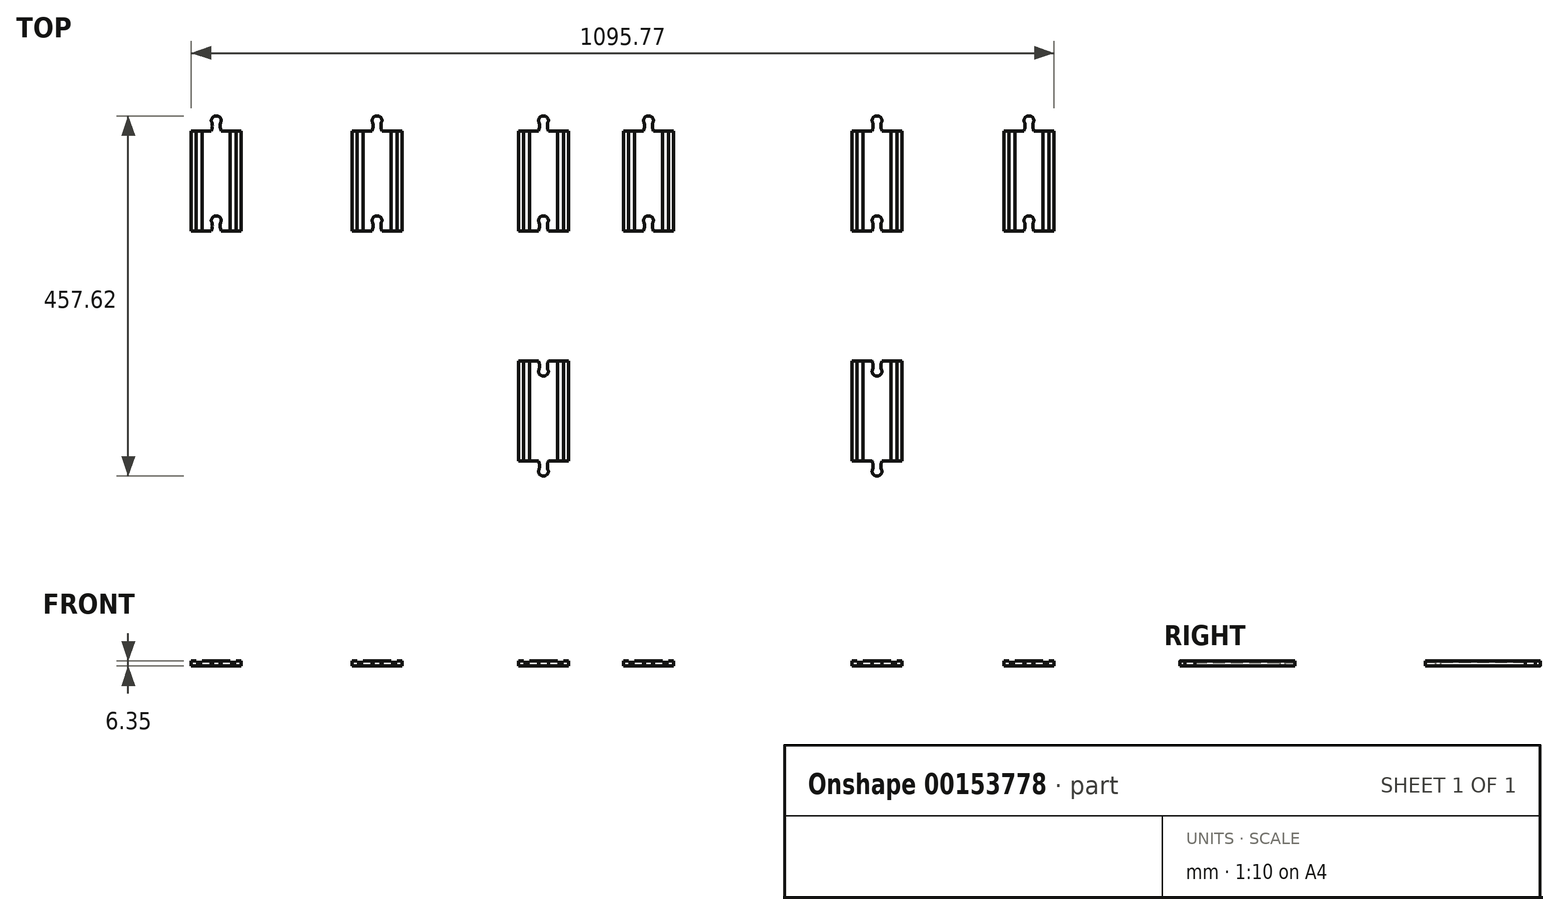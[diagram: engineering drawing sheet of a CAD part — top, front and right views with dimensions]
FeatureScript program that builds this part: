
annotation { "Feature Type Name" : "Feature", "Feature Type Description" : "" }
export const myFeature = defineFeature(function(context is Context, id is Id, definition is map)
    precondition{}
    {
        {
            var Q0;
            Q0=qCreatedBy(makeId("Top.planeOp"),FACE);
            var sketch = newSketch(context, id + "F0", { "sketchPlane" : qUnion([Q0])});
            skLineSegment(sketch, "E0", {"start": v(-44.88, 90.72) * mm, "end": v(-44.88, -36.28) * mm});
            skLineSegment(sketch, "E1", {"start": v(-44.88, -36.28) * mm, "end": v(-19.48, -36.28) * mm});
            skLineSegment(sketch, "E2", {"start": v(18.62, -36.28) * mm, "end": v(18.62, 90.72) * mm});
            skLineSegment(sketch, "E3", {"start": v(18.62, 90.72) * mm, "end": v(-6.78, 90.72) * mm});
            skArc(sketch, "E4", {"start": v(-6.78, 103.42) * mm, "mid": v(-13.13, 109.77) * mm, "end": v(-19.48, 103.42) * mm});
            skArc(sketch, "E5", {"start": v(-6.78, 103.42) * mm, "mid": v(-8.16, 97.07) * mm, "end": v(-6.78, 90.72) * mm});
            skArc(sketch, "E6.MirrorCS", {"start": v(-19.48, 103.42) * mm, "mid": v(-18.09, 97.07) * mm, "end": v(-19.48, 90.72) * mm});
            skArc(sketch, "E7", {"start": v(-6.78, -23.58) * mm, "mid": v(-13.13, -17.23) * mm, "end": v(-19.48, -23.58) * mm});
            skPoint(sketch, "E8.start.orphan", {"position": v(-13.13, -36.28) * mm});
            skArc(sketch, "E9", {"start": v(-6.78, -23.58) * mm, "mid": v(-8.16, -29.93) * mm, "end": v(-6.78, -36.28) * mm});
            skArc(sketch, "E10.MirrorCS", {"start": v(-19.48, -23.58) * mm, "mid": v(-18.09, -29.93) * mm, "end": v(-19.48, -36.28) * mm});
            skLineSegment(sketch, "E11.trimOffspring", {"start": v(-6.78, -36.28) * mm, "end": v(18.62, -36.28) * mm});
            skArc(sketch, "E12.MirrorCS", {"start": v(80.5, 103.42) * mm, "mid": v(81.9, 97.07) * mm, "end": v(80.5, 90.72) * mm});
            skLineSegment(sketch, "E13.MirrorCS", {"start": v(55.1, 90.72) * mm, "end": v(80.5, 90.72) * mm});
            skLineSegment(sketch, "E14.MirrorCS", {"start": v(118.6, 90.72) * mm, "end": v(118.6, -36.28) * mm});
            skLineSegment(sketch, "E15.MirrorCS", {"start": v(80.5, -36.28) * mm, "end": v(55.1, -36.28) * mm});
            skPoint(sketch, "E16.MirrorP", {"position": v(86.86, -36.28) * mm});
            skArc(sketch, "E17.MirrorCS", {"start": v(80.5, -23.58) * mm, "mid": v(81.9, -29.93) * mm, "end": v(80.5, -36.28) * mm});
            skArc(sketch, "E18.MirrorCS", {"start": v(80.5, 103.42) * mm, "mid": v(86.86, 109.77) * mm, "end": v(93.2, 103.42) * mm});
            skLineSegment(sketch, "E19.MirrorCS", {"start": v(55.1, -36.28) * mm, "end": v(55.1, 90.72) * mm});
            skArc(sketch, "E20.MirrorCS", {"start": v(93.2, -23.58) * mm, "mid": v(91.82, -29.93) * mm, "end": v(93.2, -36.28) * mm});
            skArc(sketch, "E21.MirrorCS", {"start": v(80.5, -23.58) * mm, "mid": v(86.86, -17.23) * mm, "end": v(93.2, -23.58) * mm});
            skLineSegment(sketch, "E22.MirrorCS", {"start": v(118.6, -36.28) * mm, "end": v(93.2, -36.28) * mm});
            skArc(sketch, "E23.MirrorCS", {"start": v(93.2, 103.42) * mm, "mid": v(91.82, 97.07) * mm, "end": v(93.2, 90.72) * mm});
            skArc(sketch, "E24.MirrorCS", {"start": v(197.37, -23.58) * mm, "mid": v(195.98, -29.93) * mm, "end": v(197.37, -36.28) * mm});
            skArc(sketch, "E25.MirrorCS", {"start": v(184.67, -23.58) * mm, "mid": v(186.06, -29.93) * mm, "end": v(184.67, -36.28) * mm});
            skArc(sketch, "E26.MirrorCS", {"start": v(184.67, 103.42) * mm, "mid": v(186.06, 97.07) * mm, "end": v(184.67, 90.72) * mm});
            skArc(sketch, "E27.MirrorCS", {"start": v(197.37, -23.58) * mm, "mid": v(191.02, -17.23) * mm, "end": v(184.67, -23.58) * mm});
            skArc(sketch, "E28.MirrorCS", {"start": v(197.37, 103.42) * mm, "mid": v(195.98, 97.07) * mm, "end": v(197.37, 90.72) * mm});
            skLineSegment(sketch, "E29.MirrorCS", {"start": v(197.37, -36.28) * mm, "end": v(222.77, -36.28) * mm});
            skArc(sketch, "E30.MirrorCS", {"start": v(197.37, 103.42) * mm, "mid": v(191.02, 109.77) * mm, "end": v(184.67, 103.42) * mm});
            skLineSegment(sketch, "E31.MirrorCS", {"start": v(159.27, -36.28) * mm, "end": v(184.67, -36.28) * mm});
            skLineSegment(sketch, "E32.MirrorCS", {"start": v(222.77, 90.72) * mm, "end": v(197.37, 90.72) * mm});
            skLineSegment(sketch, "E33.MirrorCS", {"start": v(222.77, -36.28) * mm, "end": v(222.77, 90.72) * mm});
            skPoint(sketch, "E34.MirrorP", {"position": v(191.02, -36.28) * mm});
            skLineSegment(sketch, "E35.MirrorCS", {"start": v(159.27, 90.72) * mm, "end": v(159.27, -36.28) * mm});
            skArc(sketch, "E36.MirrorCS", {"start": v(408.77, -23.58) * mm, "mid": v(407.39, -29.93) * mm, "end": v(408.77, -36.28) * mm});
            skArc(sketch, "E37.MirrorCS", {"start": v(396.07, -23.58) * mm, "mid": v(397.46, -29.93) * mm, "end": v(396.07, -36.28) * mm});
            skArc(sketch, "E38.MirrorCS", {"start": v(396.07, 103.42) * mm, "mid": v(402.42, 109.77) * mm, "end": v(408.77, 103.42) * mm});
            skLineSegment(sketch, "E39.MirrorCS", {"start": v(396.07, -36.28) * mm, "end": v(370.67, -36.28) * mm});
            skLineSegment(sketch, "E40.MirrorCS", {"start": v(434.17, -36.28) * mm, "end": v(408.77, -36.28) * mm});
            skArc(sketch, "E41.MirrorCS", {"start": v(396.07, -23.58) * mm, "mid": v(402.42, -17.23) * mm, "end": v(408.77, -23.58) * mm});
            skArc(sketch, "E42.MirrorCS", {"start": v(408.77, 103.42) * mm, "mid": v(407.39, 97.07) * mm, "end": v(408.77, 90.72) * mm});
            skArc(sketch, "E43.MirrorCS", {"start": v(396.07, 103.42) * mm, "mid": v(397.46, 97.07) * mm, "end": v(396.07, 90.72) * mm});
            skLineSegment(sketch, "E44.MirrorCS", {"start": v(370.67, 90.72) * mm, "end": v(396.07, 90.72) * mm});
            skLineSegment(sketch, "E45.MirrorCS", {"start": v(370.67, -36.28) * mm, "end": v(370.67, 90.72) * mm});
            skPoint(sketch, "E46.MirrorP", {"position": v(402.42, -36.28) * mm});
            skLineSegment(sketch, "E47.MirrorCS", {"start": v(434.17, 90.72) * mm, "end": v(434.17, -36.28) * mm});
            skArc(sketch, "E48.MirrorCS", {"start": v(542.2, 103.42) * mm, "mid": v(540.8, 97.07) * mm, "end": v(542.2, 90.72) * mm});
            skArc(sketch, "E49.MirrorCS", {"start": v(542.2, -23.58) * mm, "mid": v(540.8, -29.93) * mm, "end": v(542.2, -36.28) * mm});
            skArc(sketch, "E50.MirrorCS", {"start": v(542.2, 103.42) * mm, "mid": v(535.84, 109.77) * mm, "end": v(529.5, 103.42) * mm});
            skArc(sketch, "E51.MirrorCS", {"start": v(529.5, 103.42) * mm, "mid": v(530.88, 97.07) * mm, "end": v(529.5, 90.72) * mm});
            skArc(sketch, "E52.MirrorCS", {"start": v(529.5, -23.58) * mm, "mid": v(530.88, -29.93) * mm, "end": v(529.5, -36.28) * mm});
            skLineSegment(sketch, "E53.MirrorCS", {"start": v(567.6, 90.72) * mm, "end": v(542.2, 90.72) * mm});
            skArc(sketch, "E54.MirrorCS", {"start": v(542.2, -23.58) * mm, "mid": v(535.84, -17.23) * mm, "end": v(529.5, -23.58) * mm});
            skLineSegment(sketch, "E55.MirrorCS", {"start": v(504.1, -36.28) * mm, "end": v(529.5, -36.28) * mm});
            skLineSegment(sketch, "E56.MirrorCS", {"start": v(542.2, -36.28) * mm, "end": v(567.6, -36.28) * mm});
            skLineSegment(sketch, "E57.MirrorCS", {"start": v(504.1, 90.72) * mm, "end": v(504.1, -36.28) * mm});
            skLineSegment(sketch, "E58.MirrorCS", {"start": v(567.6, -36.28) * mm, "end": v(567.6, 90.72) * mm});
            skPoint(sketch, "E59.MirrorP", {"position": v(535.84, -36.28) * mm});
            skArc(sketch, "E60.MirrorCS", {"start": v(832.53, -23.58) * mm, "mid": v(831.14, -29.93) * mm, "end": v(832.53, -36.28) * mm});
            skArc(sketch, "E61.MirrorCS", {"start": v(819.83, -23.58) * mm, "mid": v(821.22, -29.93) * mm, "end": v(819.83, -36.28) * mm});
            skArc(sketch, "E62.MirrorCS", {"start": v(819.83, -23.58) * mm, "mid": v(826.18, -17.23) * mm, "end": v(832.53, -23.58) * mm});
            skLineSegment(sketch, "E63.MirrorCS", {"start": v(857.93, -36.28) * mm, "end": v(832.53, -36.28) * mm});
            skArc(sketch, "E64.MirrorCS", {"start": v(819.83, 103.42) * mm, "mid": v(821.22, 97.07) * mm, "end": v(819.83, 90.72) * mm});
            skArc(sketch, "E65.MirrorCS", {"start": v(832.53, 103.42) * mm, "mid": v(831.14, 97.07) * mm, "end": v(832.53, 90.72) * mm});
            skArc(sketch, "E66.MirrorCS", {"start": v(819.83, 103.42) * mm, "mid": v(826.18, 109.77) * mm, "end": v(832.53, 103.42) * mm});
            skLineSegment(sketch, "E67.MirrorCS", {"start": v(819.83, -36.28) * mm, "end": v(794.43, -36.28) * mm});
            skLineSegment(sketch, "E68.MirrorCS", {"start": v(794.43, 90.72) * mm, "end": v(819.83, 90.72) * mm});
            skPoint(sketch, "E69.MirrorP", {"position": v(826.18, -36.28) * mm});
            skLineSegment(sketch, "E70.MirrorCS", {"start": v(857.93, 90.72) * mm, "end": v(857.93, -36.28) * mm});
            skLineSegment(sketch, "E71.MirrorCS", {"start": v(794.43, -36.28) * mm, "end": v(794.43, 90.72) * mm});
            skArc(sketch, "E72.MirrorCS", {"start": v(819.83, -341.5) * mm, "mid": v(821.22, -335.15) * mm, "end": v(819.83, -328.8) * mm});
            skArc(sketch, "E73.MirrorCS", {"start": v(396.07, -214.5) * mm, "mid": v(397.46, -208.15) * mm, "end": v(396.07, -201.8) * mm});
            skArc(sketch, "E74.MirrorCS", {"start": v(93.2, -214.5) * mm, "mid": v(91.82, -208.15) * mm, "end": v(93.2, -201.8) * mm});
            skArc(sketch, "E75.MirrorCS", {"start": v(832.53, -341.5) * mm, "mid": v(831.14, -335.15) * mm, "end": v(832.53, -328.8) * mm});
            skArc(sketch, "E76.MirrorCS", {"start": v(408.77, -214.5) * mm, "mid": v(407.39, -208.15) * mm, "end": v(408.77, -201.8) * mm});
            skArc(sketch, "E77.MirrorCS", {"start": v(197.37, -214.5) * mm, "mid": v(191.02, -220.85) * mm, "end": v(184.67, -214.5) * mm});
            skArc(sketch, "E78.MirrorCS", {"start": v(80.5, -214.5) * mm, "mid": v(86.86, -220.85) * mm, "end": v(93.2, -214.5) * mm});
            skArc(sketch, "E79.MirrorCS", {"start": v(819.83, -341.5) * mm, "mid": v(826.18, -347.85) * mm, "end": v(832.53, -341.5) * mm});
            skArc(sketch, "E80.MirrorCS", {"start": v(819.83, -214.5) * mm, "mid": v(821.22, -208.15) * mm, "end": v(819.83, -201.8) * mm});
            skArc(sketch, "E81.MirrorCS", {"start": v(542.2, -214.5) * mm, "mid": v(540.8, -208.15) * mm, "end": v(542.2, -201.8) * mm});
            skArc(sketch, "E82.MirrorCS", {"start": v(197.37, -214.5) * mm, "mid": v(195.98, -208.15) * mm, "end": v(197.37, -201.8) * mm});
            skArc(sketch, "E83.MirrorCS", {"start": v(80.5, -214.5) * mm, "mid": v(81.9, -208.15) * mm, "end": v(80.5, -201.8) * mm});
            skArc(sketch, "E84.MirrorCS", {"start": v(832.53, -214.5) * mm, "mid": v(831.14, -208.15) * mm, "end": v(832.53, -201.8) * mm});
            skArc(sketch, "E85.MirrorCS", {"start": v(184.67, -214.5) * mm, "mid": v(186.06, -208.15) * mm, "end": v(184.67, -201.8) * mm});
            skArc(sketch, "E86.MirrorCS", {"start": v(529.5, -214.5) * mm, "mid": v(530.88, -208.15) * mm, "end": v(529.5, -201.8) * mm});
            skLineSegment(sketch, "E87.MirrorCS", {"start": v(197.37, -201.8) * mm, "end": v(222.77, -201.8) * mm});
            skArc(sketch, "E88.MirrorCS", {"start": v(542.2, -214.5) * mm, "mid": v(535.84, -220.85) * mm, "end": v(529.5, -214.5) * mm});
            skArc(sketch, "E89.MirrorCS", {"start": v(197.37, -341.5) * mm, "mid": v(195.98, -335.15) * mm, "end": v(197.37, -328.8) * mm});
            skLineSegment(sketch, "E90.MirrorCS", {"start": v(857.93, -201.8) * mm, "end": v(832.53, -201.8) * mm});
            skArc(sketch, "E91.MirrorCS", {"start": v(80.5, -341.5) * mm, "mid": v(86.86, -347.85) * mm, "end": v(93.2, -341.5) * mm});
            skLineSegment(sketch, "E92.MirrorCS", {"start": v(504.1, -201.8) * mm, "end": v(529.5, -201.8) * mm});
            skArc(sketch, "E93.MirrorCS", {"start": v(396.07, -341.5) * mm, "mid": v(402.42, -347.85) * mm, "end": v(408.77, -341.5) * mm});
            skArc(sketch, "E94.MirrorCS", {"start": v(542.2, -341.5) * mm, "mid": v(540.8, -335.15) * mm, "end": v(542.2, -328.8) * mm});
            skArc(sketch, "E95.MirrorCS", {"start": v(197.37, -341.5) * mm, "mid": v(191.02, -347.85) * mm, "end": v(184.67, -341.5) * mm});
            skLineSegment(sketch, "E96.MirrorCS", {"start": v(567.6, -328.8) * mm, "end": v(542.2, -328.8) * mm});
            skLineSegment(sketch, "E97.MirrorCS", {"start": v(370.67, -328.8) * mm, "end": v(396.07, -328.8) * mm});
            skArc(sketch, "E98.MirrorCS", {"start": v(819.83, -214.5) * mm, "mid": v(826.18, -220.85) * mm, "end": v(832.53, -214.5) * mm});
            skLineSegment(sketch, "E99.MirrorCS", {"start": v(396.07, -201.8) * mm, "end": v(370.67, -201.8) * mm});
            skLineSegment(sketch, "E100.MirrorCS", {"start": v(542.2, -201.8) * mm, "end": v(567.6, -201.8) * mm});
            skArc(sketch, "E101.MirrorCS", {"start": v(93.2, -341.5) * mm, "mid": v(91.82, -335.15) * mm, "end": v(93.2, -328.8) * mm});
            skArc(sketch, "E102.MirrorCS", {"start": v(396.07, -341.5) * mm, "mid": v(397.46, -335.15) * mm, "end": v(396.07, -328.8) * mm});
            skLineSegment(sketch, "E103.MirrorCS", {"start": v(794.43, -328.8) * mm, "end": v(819.83, -328.8) * mm});
            skArc(sketch, "E104.MirrorCS", {"start": v(529.5, -341.5) * mm, "mid": v(530.88, -335.15) * mm, "end": v(529.5, -328.8) * mm});
            skArc(sketch, "E105.MirrorCS", {"start": v(184.67, -341.5) * mm, "mid": v(186.06, -335.15) * mm, "end": v(184.67, -328.8) * mm});
            skArc(sketch, "E106.MirrorCS", {"start": v(396.07, -214.5) * mm, "mid": v(402.42, -220.85) * mm, "end": v(408.77, -214.5) * mm});
            skLineSegment(sketch, "E107.MirrorCS", {"start": v(55.1, -328.8) * mm, "end": v(80.5, -328.8) * mm});
            skLineSegment(sketch, "E108.MirrorCS", {"start": v(159.27, -201.8) * mm, "end": v(184.67, -201.8) * mm});
            skLineSegment(sketch, "E109.MirrorCS", {"start": v(80.5, -201.8) * mm, "end": v(55.1, -201.8) * mm});
            skLineSegment(sketch, "E110.MirrorCS", {"start": v(434.17, -201.8) * mm, "end": v(408.77, -201.8) * mm});
            skLineSegment(sketch, "E111.MirrorCS", {"start": v(819.83, -201.8) * mm, "end": v(794.43, -201.8) * mm});
            skArc(sketch, "E112.MirrorCS", {"start": v(408.77, -341.5) * mm, "mid": v(407.39, -335.15) * mm, "end": v(408.77, -328.8) * mm});
            skLineSegment(sketch, "E113.MirrorCS", {"start": v(222.77, -328.8) * mm, "end": v(197.37, -328.8) * mm});
            skArc(sketch, "E114.MirrorCS", {"start": v(80.5, -341.5) * mm, "mid": v(81.9, -335.15) * mm, "end": v(80.5, -328.8) * mm});
            skLineSegment(sketch, "E115.MirrorCS", {"start": v(118.6, -201.8) * mm, "end": v(93.2, -201.8) * mm});
            skArc(sketch, "E116.MirrorCS", {"start": v(542.2, -341.5) * mm, "mid": v(535.84, -347.85) * mm, "end": v(529.5, -341.5) * mm});
            skLineSegment(sketch, "E117.MirrorCS", {"start": v(434.17, -328.8) * mm, "end": v(434.17, -201.8) * mm});
            skLineSegment(sketch, "E118.MirrorCS", {"start": v(55.1, -201.8) * mm, "end": v(55.1, -328.8) * mm});
            skLineSegment(sketch, "E119.MirrorCS", {"start": v(370.67, -201.8) * mm, "end": v(370.67, -328.8) * mm});
            skPoint(sketch, "E120.MirrorP", {"position": v(86.86, -201.8) * mm});
            skLineSegment(sketch, "E121.MirrorCS", {"start": v(794.43, -201.8) * mm, "end": v(794.43, -328.8) * mm});
            skPoint(sketch, "E122.MirrorP", {"position": v(191.02, -201.8) * mm});
            skPoint(sketch, "E123.MirrorP", {"position": v(535.84, -201.8) * mm});
            skPoint(sketch, "E124.MirrorP", {"position": v(402.42, -201.8) * mm});
            skLineSegment(sketch, "E125.MirrorCS", {"start": v(567.6, -201.8) * mm, "end": v(567.6, -328.8) * mm});
            skLineSegment(sketch, "E126.MirrorCS", {"start": v(222.77, -201.8) * mm, "end": v(222.77, -328.8) * mm});
            skLineSegment(sketch, "E127.MirrorCS", {"start": v(118.6, -328.8) * mm, "end": v(118.6, -201.8) * mm});
            skPoint(sketch, "E128.MirrorP", {"position": v(826.18, -201.8) * mm});
            skLineSegment(sketch, "E129.MirrorCS", {"start": v(504.1, -328.8) * mm, "end": v(504.1, -201.8) * mm});
            skLineSegment(sketch, "E130.MirrorCS", {"start": v(159.27, -328.8) * mm, "end": v(159.27, -201.8) * mm});
            skLineSegment(sketch, "E131.MirrorCS", {"start": v(857.93, -328.8) * mm, "end": v(857.93, -201.8) * mm});
            skArc(sketch, "E132.MirrorCS", {"start": v(-6.78, -341.5) * mm, "mid": v(-13.13, -347.85) * mm, "end": v(-19.48, -341.5) * mm});
            skArc(sketch, "E133.MirrorCS", {"start": v(-19.48, -214.5) * mm, "mid": v(-18.09, -208.15) * mm, "end": v(-19.48, -201.8) * mm});
            skArc(sketch, "E134.MirrorCS", {"start": v(-6.78, -214.5) * mm, "mid": v(-13.13, -220.85) * mm, "end": v(-19.48, -214.5) * mm});
            skLineSegment(sketch, "E135.MirrorCS", {"start": v(-6.78, -201.8) * mm, "end": v(18.62, -201.8) * mm});
            skArc(sketch, "E136.MirrorCS", {"start": v(-6.78, -214.5) * mm, "mid": v(-8.16, -208.15) * mm, "end": v(-6.78, -201.8) * mm});
            skArc(sketch, "E137.MirrorCS", {"start": v(-19.48, -341.5) * mm, "mid": v(-18.09, -335.15) * mm, "end": v(-19.48, -328.8) * mm});
            skArc(sketch, "E138.MirrorCS", {"start": v(-6.78, -341.5) * mm, "mid": v(-8.16, -335.15) * mm, "end": v(-6.78, -328.8) * mm});
            skLineSegment(sketch, "E139.MirrorCS", {"start": v(18.62, -328.8) * mm, "end": v(-6.78, -328.8) * mm});
            skLineSegment(sketch, "E140.MirrorCS", {"start": v(-44.88, -201.8) * mm, "end": v(-19.48, -201.8) * mm});
            skLineSegment(sketch, "E141.MirrorCS", {"start": v(18.62, -201.8) * mm, "end": v(18.62, -328.8) * mm});
            skLineSegment(sketch, "E142.MirrorCS", {"start": v(-44.88, -328.8) * mm, "end": v(-44.88, -201.8) * mm});
            skPoint(sketch, "E143.MirrorP", {"position": v(-13.13, -201.8) * mm});
            skLineSegment(sketch, "E144.trimOffspring", {"start": v(-19.48, 90.72) * mm, "end": v(-44.88, 90.72) * mm});
            skLineSegment(sketch, "E145.trimOffspring", {"start": v(93.2, 90.72) * mm, "end": v(118.6, 90.72) * mm});
            skLineSegment(sketch, "E146.trimOffspring", {"start": v(184.67, 90.72) * mm, "end": v(159.27, 90.72) * mm});
            skLineSegment(sketch, "E147.trimOffspring", {"start": v(408.77, 90.72) * mm, "end": v(434.17, 90.72) * mm});
            skLineSegment(sketch, "E148.trimOffspring", {"start": v(529.5, 90.72) * mm, "end": v(504.1, 90.72) * mm});
            skLineSegment(sketch, "E149.trimOffspring", {"start": v(832.53, 90.72) * mm, "end": v(857.93, 90.72) * mm});
            skLineSegment(sketch, "E150.trimOffspring", {"start": v(832.53, -328.8) * mm, "end": v(857.93, -328.8) * mm});
            skLineSegment(sketch, "E151.trimOffspring", {"start": v(529.5, -328.8) * mm, "end": v(504.1, -328.8) * mm});
            skLineSegment(sketch, "E152.trimOffspring", {"start": v(408.77, -328.8) * mm, "end": v(434.17, -328.8) * mm});
            skLineSegment(sketch, "E153.trimOffspring", {"start": v(184.67, -328.8) * mm, "end": v(159.27, -328.8) * mm});
            skLineSegment(sketch, "E154.trimOffspring", {"start": v(93.2, -328.8) * mm, "end": v(118.6, -328.8) * mm});
            skLineSegment(sketch, "E155.trimOffspring", {"start": v(-19.48, -328.8) * mm, "end": v(-44.88, -328.8) * mm});
            skLineSegment(sketch, "E156", {"start": v(922.66, 120.17) * mm, "end": v(922.66, -61.86) * mm});
            skArc(sketch, "E157.MirrorCS", {"start": v(1025.49, -23.58) * mm, "mid": v(1024.1, -29.93) * mm, "end": v(1025.49, -36.28) * mm});
            skArc(sketch, "E158.MirrorCS", {"start": v(1012.79, -23.58) * mm, "mid": v(1014.17, -29.93) * mm, "end": v(1012.79, -36.28) * mm});
            skArc(sketch, "E159.MirrorCS", {"start": v(1025.49, 103.42) * mm, "mid": v(1024.1, 97.07) * mm, "end": v(1025.49, 90.72) * mm});
            skArc(sketch, "E160.MirrorCS", {"start": v(1012.79, 103.42) * mm, "mid": v(1014.17, 97.07) * mm, "end": v(1012.79, 90.72) * mm});
            skLineSegment(sketch, "E161.MirrorCS", {"start": v(1025.49, -36.28) * mm, "end": v(1050.89, -36.28) * mm});
            skLineSegment(sketch, "E162.MirrorCS", {"start": v(1050.89, 90.72) * mm, "end": v(1025.49, 90.72) * mm});
            skArc(sketch, "E163.MirrorCS", {"start": v(1025.49, -23.58) * mm, "mid": v(1019.14, -17.23) * mm, "end": v(1012.79, -23.58) * mm});
            skArc(sketch, "E164.MirrorCS", {"start": v(1025.49, 103.42) * mm, "mid": v(1019.14, 109.77) * mm, "end": v(1012.79, 103.42) * mm});
            skLineSegment(sketch, "E165.MirrorCS", {"start": v(1012.79, 90.72) * mm, "end": v(987.39, 90.72) * mm});
            skLineSegment(sketch, "E166.MirrorCS", {"start": v(987.39, -36.28) * mm, "end": v(1012.79, -36.28) * mm});
            skPoint(sketch, "E167.MirrorP", {"position": v(1019.14, -36.28) * mm});
            skLineSegment(sketch, "E168.MirrorCS", {"start": v(987.39, 90.72) * mm, "end": v(987.39, -36.28) * mm});
            skLineSegment(sketch, "E169.MirrorCS", {"start": v(1050.89, -36.28) * mm, "end": v(1050.89, 90.72) * mm});
            skSolve(sketch);
        }
        {
            var Q0;
            Q0=makeQuery(id+"F0.imprint","IMPRINT",FACE,{"disambiguationData":[TD([[makeQuery(id+"F0.imprint","IMPRINT",EDGE,{"derivedFrom":sQuery(id+"F0.wireOp",EDGE,"E0")}),1.0]])]});
            var Q1;
            Q1=makeQuery(id+"F0.imprint","IMPRINT",FACE,{"disambiguationData":[TD([[makeQuery(id+"F0.imprint","IMPRINT",EDGE,{"derivedFrom":sQuery(id+"F0.wireOp",EDGE,"E12.MirrorCS")}),1.0]])]});
            var Q2;
            Q2=makeQuery(id+"F0.imprint","IMPRINT",FACE,{"disambiguationData":[TD([[makeQuery(id+"F0.imprint","IMPRINT",EDGE,{"derivedFrom":sQuery(id+"F0.wireOp",EDGE,"E24.MirrorCS")}),1.0]])]});
            var Q3;
            Q3=makeQuery(id+"F0.imprint","IMPRINT",FACE,{"disambiguationData":[TD([[makeQuery(id+"F0.imprint","IMPRINT",EDGE,{"derivedFrom":sQuery(id+"F0.wireOp",EDGE,"E36.MirrorCS")}),1.0]])]});
            var Q4;
            Q4=makeQuery(id+"F0.imprint","IMPRINT",FACE,{"disambiguationData":[TD([[makeQuery(id+"F0.imprint","IMPRINT",EDGE,{"derivedFrom":sQuery(id+"F0.wireOp",EDGE,"E48.MirrorCS")}),-1.0]])]});
            var Q5;
            Q5=makeQuery(id+"F0.imprint","IMPRINT",FACE,{"disambiguationData":[TD([[makeQuery(id+"F0.imprint","IMPRINT",EDGE,{"derivedFrom":sQuery(id+"F0.wireOp",EDGE,"E132.MirrorCS")}),-1.0]])]});
            var Q6;
            Q6=makeQuery(id+"F0.imprint","IMPRINT",FACE,{"disambiguationData":[TD([[makeQuery(id+"F0.imprint","IMPRINT",EDGE,{"derivedFrom":sQuery(id+"F0.wireOp",EDGE,"E74.MirrorCS")}),-1.0]])]});
            var Q7;
            Q7=makeQuery(id+"F0.imprint","IMPRINT",FACE,{"disambiguationData":[TD([[makeQuery(id+"F0.imprint","IMPRINT",EDGE,{"derivedFrom":sQuery(id+"F0.wireOp",EDGE,"E77.MirrorCS")}),1.0]])]});
            var Q8;
            Q8=makeQuery(id+"F0.imprint","IMPRINT",FACE,{"disambiguationData":[TD([[makeQuery(id+"F0.imprint","IMPRINT",EDGE,{"derivedFrom":sQuery(id+"F0.wireOp",EDGE,"E73.MirrorCS")}),1.0]])]});
            var Q9;
            Q9=makeQuery(id+"F0.imprint","IMPRINT",FACE,{"disambiguationData":[TD([[makeQuery(id+"F0.imprint","IMPRINT",EDGE,{"derivedFrom":sQuery(id+"F0.wireOp",EDGE,"E81.MirrorCS")}),-1.0]])]});
            var Q10;
            Q10=makeQuery(id+"F0.imprint","IMPRINT",FACE,{"disambiguationData":[TD([[makeQuery(id+"F0.imprint","IMPRINT",EDGE,{"derivedFrom":sQuery(id+"F0.wireOp",EDGE,"E60.MirrorCS")}),1.0]])]});
            var Q11;
            Q11=makeQuery(id+"F0.imprint","IMPRINT",FACE,{"disambiguationData":[TD([[makeQuery(id+"F0.imprint","IMPRINT",EDGE,{"derivedFrom":sQuery(id+"F0.wireOp",EDGE,"E72.MirrorCS")}),-1.0]])]});
            var Q12;
            Q12=makeQuery(id+"F0.imprint","IMPRINT",FACE,{"disambiguationData":[TD([[makeQuery(id+"F0.imprint","IMPRINT",EDGE,{"derivedFrom":sQuery(id+"F0.wireOp",EDGE,"E157.MirrorCS")}),1.0]])]});
            extrude(context, id + "F1", {"entities" : qUnion([Q0, Q1, Q2, Q3, Q4, Q5, Q6, Q7, Q8, Q9, Q10, Q11, Q12]), "depth" : 6.35 * mm});
        }
        {
            var Q0;
            Q0=makeQuery(id+"F1.opExtrude","CAP_FACE",FACE,{"disambiguationData":[OSD([sQuery(id+"F0.wireOp",EDGE,"E0"),sQuery(id+"F0.wireOp",EDGE,"E1"),sQuery(id+"F0.wireOp",EDGE,"E2"),sQuery(id+"F0.wireOp",EDGE,"E3"),sQuery(id+"F0.wireOp",EDGE,"E4"),sQuery(id+"F0.wireOp",EDGE,"E5"),sQuery(id+"F0.wireOp",EDGE,"E6.MirrorCS"),sQuery(id+"F0.wireOp",EDGE,"E7"),sQuery(id+"F0.wireOp",EDGE,"E9"),sQuery(id+"F0.wireOp",EDGE,"E10.MirrorCS"),sQuery(id+"F0.wireOp",EDGE,"E11.trimOffspring"),sQuery(id+"F0.wireOp",EDGE,"E144.trimOffspring")])],"isStart":false});
            var sketch = newSketch(context, id + "F2", { "sketchPlane" : qUnion([Q0])});
            skLineSegment(sketch, "E170.12", {"start": v(857.93, -328.8) * mm, "end": v(857.93, -201.8) * mm});
            skLineSegment(sketch, "E170.13", {"start": v(794.43, -201.8) * mm, "end": v(794.43, -328.8) * mm});
            skLineSegment(sketch, "E171.0", {"start": v(-38.53, 90.72) * mm, "end": v(-38.53, -36.28) * mm});
            skLineSegment(sketch, "E172.0", {"start": v(-30.9, 90.72) * mm, "end": v(-30.9, -36.28) * mm});
            skLineSegment(sketch, "E173", {"start": v(4.65, 90.72) * mm, "end": v(4.65, -36.28) * mm});
            skLineSegment(sketch, "E174", {"start": v(12.27, 90.72) * mm, "end": v(12.27, -36.28) * mm});
            skLineSegment(sketch, "E175", {"start": v(-38.53, -36.28) * mm, "end": v(-30.9, -36.28) * mm});
            skLineSegment(sketch, "E176", {"start": v(-30.9, 90.72) * mm, "end": v(-38.53, 90.72) * mm});
            skLineSegment(sketch, "E177", {"start": v(4.65, 90.72) * mm, "end": v(12.27, 90.72) * mm});
            skLineSegment(sketch, "E178", {"start": v(12.27, -36.28) * mm, "end": v(4.65, -36.28) * mm});
            skLineSegment(sketch, "E179.MirrorCS", {"start": v(61.46, 90.72) * mm, "end": v(61.46, -36.28) * mm});
            skLineSegment(sketch, "E180.MirrorCS", {"start": v(69.08, 90.72) * mm, "end": v(69.08, -36.28) * mm});
            skLineSegment(sketch, "E181.MirrorCS", {"start": v(61.46, -36.28) * mm, "end": v(69.08, -36.28) * mm});
            skLineSegment(sketch, "E182.MirrorCS", {"start": v(69.08, 90.72) * mm, "end": v(61.46, 90.72) * mm});
            skLineSegment(sketch, "E183.MirrorCS", {"start": v(112.26, -36.28) * mm, "end": v(104.64, -36.28) * mm});
            skLineSegment(sketch, "E184.MirrorCS", {"start": v(104.64, 90.72) * mm, "end": v(104.64, -36.28) * mm});
            skLineSegment(sketch, "E185.MirrorCS", {"start": v(112.26, 90.72) * mm, "end": v(112.26, -36.28) * mm});
            skLineSegment(sketch, "E186.MirrorCS", {"start": v(104.64, 90.72) * mm, "end": v(112.26, 90.72) * mm});
            skLineSegment(sketch, "E187.MirrorCS", {"start": v(165.62, 90.72) * mm, "end": v(165.62, -36.28) * mm});
            skLineSegment(sketch, "E188.MirrorCS", {"start": v(173.24, 90.72) * mm, "end": v(173.24, -36.28) * mm});
            skLineSegment(sketch, "E189.MirrorCS", {"start": v(208.8, 90.72) * mm, "end": v(208.8, -36.28) * mm});
            skLineSegment(sketch, "E190.MirrorCS", {"start": v(216.42, 90.72) * mm, "end": v(216.42, -36.28) * mm});
            skLineSegment(sketch, "E191.MirrorCS", {"start": v(173.24, 90.72) * mm, "end": v(165.62, 90.72) * mm});
            skLineSegment(sketch, "E192.MirrorCS", {"start": v(165.62, -36.28) * mm, "end": v(173.24, -36.28) * mm});
            skLineSegment(sketch, "E193.MirrorCS", {"start": v(216.42, -36.28) * mm, "end": v(208.8, -36.28) * mm});
            skLineSegment(sketch, "E194.MirrorCS", {"start": v(208.8, 90.72) * mm, "end": v(216.42, 90.72) * mm});
            skLineSegment(sketch, "E195.MirrorCS", {"start": v(377.02, 90.72) * mm, "end": v(377.02, -36.28) * mm});
            skLineSegment(sketch, "E196.MirrorCS", {"start": v(384.64, 90.72) * mm, "end": v(384.64, -36.28) * mm});
            skLineSegment(sketch, "E197.MirrorCS", {"start": v(420.2, 90.72) * mm, "end": v(420.2, -36.28) * mm});
            skLineSegment(sketch, "E198.MirrorCS", {"start": v(427.82, 90.72) * mm, "end": v(427.82, -36.28) * mm});
            skLineSegment(sketch, "E199.MirrorCS", {"start": v(420.2, 90.72) * mm, "end": v(427.82, 90.72) * mm});
            skLineSegment(sketch, "E200.MirrorCS", {"start": v(384.64, 90.72) * mm, "end": v(377.02, 90.72) * mm});
            skLineSegment(sketch, "E201.MirrorCS", {"start": v(377.02, -36.28) * mm, "end": v(384.64, -36.28) * mm});
            skLineSegment(sketch, "E202.MirrorCS", {"start": v(427.82, -36.28) * mm, "end": v(420.2, -36.28) * mm});
            skLineSegment(sketch, "E203.MirrorCS", {"start": v(510.44, 90.72) * mm, "end": v(510.44, -36.28) * mm});
            skLineSegment(sketch, "E204.MirrorCS", {"start": v(518.06, 90.72) * mm, "end": v(518.06, -36.28) * mm});
            skLineSegment(sketch, "E205.MirrorCS", {"start": v(518.06, 90.72) * mm, "end": v(510.44, 90.72) * mm});
            skLineSegment(sketch, "E206.MirrorCS", {"start": v(553.62, 90.72) * mm, "end": v(553.62, -36.28) * mm});
            skLineSegment(sketch, "E207.MirrorCS", {"start": v(561.24, 90.72) * mm, "end": v(561.24, -36.28) * mm});
            skLineSegment(sketch, "E208.MirrorCS", {"start": v(553.62, 90.72) * mm, "end": v(561.24, 90.72) * mm});
            skLineSegment(sketch, "E209.MirrorCS", {"start": v(800.78, 90.72) * mm, "end": v(800.78, -36.28) * mm});
            skLineSegment(sketch, "E210.MirrorCS", {"start": v(808.4, 90.72) * mm, "end": v(808.4, -36.28) * mm});
            skLineSegment(sketch, "E211.MirrorCS", {"start": v(808.4, 90.72) * mm, "end": v(800.78, 90.72) * mm});
            skLineSegment(sketch, "E212.MirrorCS", {"start": v(843.96, 90.72) * mm, "end": v(851.58, 90.72) * mm});
            skLineSegment(sketch, "E213.MirrorCS", {"start": v(843.96, 90.72) * mm, "end": v(843.96, -36.28) * mm});
            skLineSegment(sketch, "E214.MirrorCS", {"start": v(851.58, 90.72) * mm, "end": v(851.58, -36.28) * mm});
            skLineSegment(sketch, "E215", {"start": v(808.4, -36.28) * mm, "end": v(800.78, -36.28) * mm});
            skLineSegment(sketch, "E216", {"start": v(851.58, -36.28) * mm, "end": v(843.96, -36.28) * mm});
            skLineSegment(sketch, "E217", {"start": v(561.24, -36.28) * mm, "end": v(553.62, -36.28) * mm});
            skLineSegment(sketch, "E218", {"start": v(518.06, -36.28) * mm, "end": v(510.44, -36.28) * mm});
            skLineSegment(sketch, "E219.MirrorCS", {"start": v(427.82, -201.8) * mm, "end": v(420.2, -201.8) * mm});
            skLineSegment(sketch, "E220.MirrorCS", {"start": v(61.46, -201.8) * mm, "end": v(69.08, -201.8) * mm});
            skLineSegment(sketch, "E221.MirrorCS", {"start": v(-38.53, -201.8) * mm, "end": v(-30.9, -201.8) * mm});
            skLineSegment(sketch, "E222.MirrorCS", {"start": v(-30.9, -328.8) * mm, "end": v(-38.53, -328.8) * mm});
            skLineSegment(sketch, "E223.MirrorCS", {"start": v(165.62, -201.8) * mm, "end": v(173.24, -201.8) * mm});
            skLineSegment(sketch, "E224.MirrorCS", {"start": v(518.06, -201.8) * mm, "end": v(510.44, -201.8) * mm});
            skLineSegment(sketch, "E225.MirrorCS", {"start": v(518.06, -328.8) * mm, "end": v(510.44, -328.8) * mm});
            skLineSegment(sketch, "E226.MirrorCS", {"start": v(173.24, -328.8) * mm, "end": v(165.62, -328.8) * mm});
            skLineSegment(sketch, "E227.MirrorCS", {"start": v(851.58, -201.8) * mm, "end": v(843.96, -201.8) * mm});
            skLineSegment(sketch, "E228.MirrorCS", {"start": v(384.64, -328.8) * mm, "end": v(377.02, -328.8) * mm});
            skLineSegment(sketch, "E229.MirrorCS", {"start": v(420.2, -328.8) * mm, "end": v(427.82, -328.8) * mm});
            skLineSegment(sketch, "E230.MirrorCS", {"start": v(377.02, -201.8) * mm, "end": v(384.64, -201.8) * mm});
            skLineSegment(sketch, "E231.MirrorCS", {"start": v(208.8, -328.8) * mm, "end": v(216.42, -328.8) * mm});
            skLineSegment(sketch, "E232.MirrorCS", {"start": v(69.08, -328.8) * mm, "end": v(61.46, -328.8) * mm});
            skLineSegment(sketch, "E233.MirrorCS", {"start": v(808.4, -328.8) * mm, "end": v(800.78, -328.8) * mm});
            skLineSegment(sketch, "E234.MirrorCS", {"start": v(4.65, -328.8) * mm, "end": v(12.27, -328.8) * mm});
            skLineSegment(sketch, "E235.MirrorCS", {"start": v(112.26, -201.8) * mm, "end": v(104.64, -201.8) * mm});
            skLineSegment(sketch, "E236.MirrorCS", {"start": v(553.62, -328.8) * mm, "end": v(561.24, -328.8) * mm});
            skLineSegment(sketch, "E237.MirrorCS", {"start": v(104.64, -328.8) * mm, "end": v(112.26, -328.8) * mm});
            skLineSegment(sketch, "E238.MirrorCS", {"start": v(843.96, -328.8) * mm, "end": v(851.58, -328.8) * mm});
            skLineSegment(sketch, "E239.MirrorCS", {"start": v(216.42, -201.8) * mm, "end": v(208.8, -201.8) * mm});
            skLineSegment(sketch, "E240.MirrorCS", {"start": v(808.4, -201.8) * mm, "end": v(800.78, -201.8) * mm});
            skLineSegment(sketch, "E241.MirrorCS", {"start": v(561.24, -201.8) * mm, "end": v(553.62, -201.8) * mm});
            skLineSegment(sketch, "E242.MirrorCS", {"start": v(12.27, -201.8) * mm, "end": v(4.65, -201.8) * mm});
            skLineSegment(sketch, "E243.MirrorCS", {"start": v(12.27, -328.8) * mm, "end": v(12.27, -201.8) * mm});
            skLineSegment(sketch, "E244.MirrorCS", {"start": v(-38.53, -328.8) * mm, "end": v(-38.53, -201.8) * mm});
            skLineSegment(sketch, "E245.MirrorCS", {"start": v(377.02, -328.8) * mm, "end": v(377.02, -201.8) * mm});
            skLineSegment(sketch, "E246.MirrorCS", {"start": v(61.46, -328.8) * mm, "end": v(61.46, -201.8) * mm});
            skLineSegment(sketch, "E247.MirrorCS", {"start": v(843.96, -328.8) * mm, "end": v(843.96, -201.8) * mm});
            skLineSegment(sketch, "E248.MirrorCS", {"start": v(420.2, -328.8) * mm, "end": v(420.2, -201.8) * mm});
            skLineSegment(sketch, "E249.MirrorCS", {"start": v(518.06, -328.8) * mm, "end": v(518.06, -201.8) * mm});
            skLineSegment(sketch, "E250.MirrorCS", {"start": v(173.24, -328.8) * mm, "end": v(173.24, -201.8) * mm});
            skLineSegment(sketch, "E251.MirrorCS", {"start": v(165.62, -328.8) * mm, "end": v(165.62, -201.8) * mm});
            skLineSegment(sketch, "E252.MirrorCS", {"start": v(510.44, -328.8) * mm, "end": v(510.44, -201.8) * mm});
            skLineSegment(sketch, "E253.MirrorCS", {"start": v(4.65, -328.8) * mm, "end": v(4.65, -201.8) * mm});
            skLineSegment(sketch, "E254.MirrorCS", {"start": v(851.58, -328.8) * mm, "end": v(851.58, -201.8) * mm});
            skLineSegment(sketch, "E255.MirrorCS", {"start": v(427.82, -328.8) * mm, "end": v(427.82, -201.8) * mm});
            skLineSegment(sketch, "E256.MirrorCS", {"start": v(208.8, -328.8) * mm, "end": v(208.8, -201.8) * mm});
            skLineSegment(sketch, "E257.MirrorCS", {"start": v(69.08, -328.8) * mm, "end": v(69.08, -201.8) * mm});
            skLineSegment(sketch, "E258.MirrorCS", {"start": v(112.26, -328.8) * mm, "end": v(112.26, -201.8) * mm});
            skLineSegment(sketch, "E259.MirrorCS", {"start": v(561.24, -328.8) * mm, "end": v(561.24, -201.8) * mm});
            skLineSegment(sketch, "E260.MirrorCS", {"start": v(-30.9, -328.8) * mm, "end": v(-30.9, -201.8) * mm});
            skLineSegment(sketch, "E261.MirrorCS", {"start": v(370.67, -201.8) * mm, "end": v(370.67, -328.8) * mm});
            skLineSegment(sketch, "E262.MirrorCS", {"start": v(434.17, -328.8) * mm, "end": v(434.17, -201.8) * mm});
            skLineSegment(sketch, "E263.MirrorCS", {"start": v(384.64, -328.8) * mm, "end": v(384.64, -201.8) * mm});
            skLineSegment(sketch, "E264.MirrorCS", {"start": v(216.42, -328.8) * mm, "end": v(216.42, -201.8) * mm});
            skLineSegment(sketch, "E265.MirrorCS", {"start": v(800.78, -328.8) * mm, "end": v(800.78, -201.8) * mm});
            skLineSegment(sketch, "E266.MirrorCS", {"start": v(553.62, -328.8) * mm, "end": v(553.62, -201.8) * mm});
            skLineSegment(sketch, "E267.MirrorCS", {"start": v(808.4, -328.8) * mm, "end": v(808.4, -201.8) * mm});
            skLineSegment(sketch, "E268.MirrorCS", {"start": v(104.64, -328.8) * mm, "end": v(104.64, -201.8) * mm});
            skLineSegment(sketch, "E269.MirrorCS", {"start": v(567.6, -201.8) * mm, "end": v(567.6, -328.8) * mm});
            skLineSegment(sketch, "E270.MirrorCS", {"start": v(504.1, -328.8) * mm, "end": v(504.1, -201.8) * mm});
            skLineSegment(sketch, "E271.MirrorCS", {"start": v(222.77, -201.8) * mm, "end": v(222.77, -328.8) * mm});
            skLineSegment(sketch, "E272.0", {"start": v(922.66, 120.17) * mm, "end": v(922.66, -61.86) * mm});
            skLineSegment(sketch, "E273.MirrorCS", {"start": v(993.74, -36.28) * mm, "end": v(1001.36, -36.28) * mm});
            skLineSegment(sketch, "E274.MirrorCS", {"start": v(1001.36, 90.72) * mm, "end": v(993.74, 90.72) * mm});
            skLineSegment(sketch, "E275.MirrorCS", {"start": v(1036.92, -36.28) * mm, "end": v(1044.54, -36.28) * mm});
            skLineSegment(sketch, "E276.MirrorCS", {"start": v(1036.92, 90.72) * mm, "end": v(1044.54, 90.72) * mm});
            skLineSegment(sketch, "E277.MirrorCS", {"start": v(1044.54, 90.72) * mm, "end": v(1044.54, -36.28) * mm});
            skLineSegment(sketch, "E278.MirrorCS", {"start": v(1036.92, 90.72) * mm, "end": v(1036.92, -36.28) * mm});
            skLineSegment(sketch, "E279.MirrorCS", {"start": v(1001.36, 90.72) * mm, "end": v(1001.36, -36.28) * mm});
            skLineSegment(sketch, "E280.MirrorCS", {"start": v(993.74, 90.72) * mm, "end": v(993.74, -36.28) * mm});
            skSolve(sketch);
        }
        {
            var Q0;
            Q0 = qSketchRegion(id + "F2", true);
            extrude(context, id + "F3", {"entities" : qUnion([Q0]), "operationType" : NewBodyOperationType.REMOVE, "oppositeDirection" : true, "depth" : 1.9 * mm});
        }
    });
